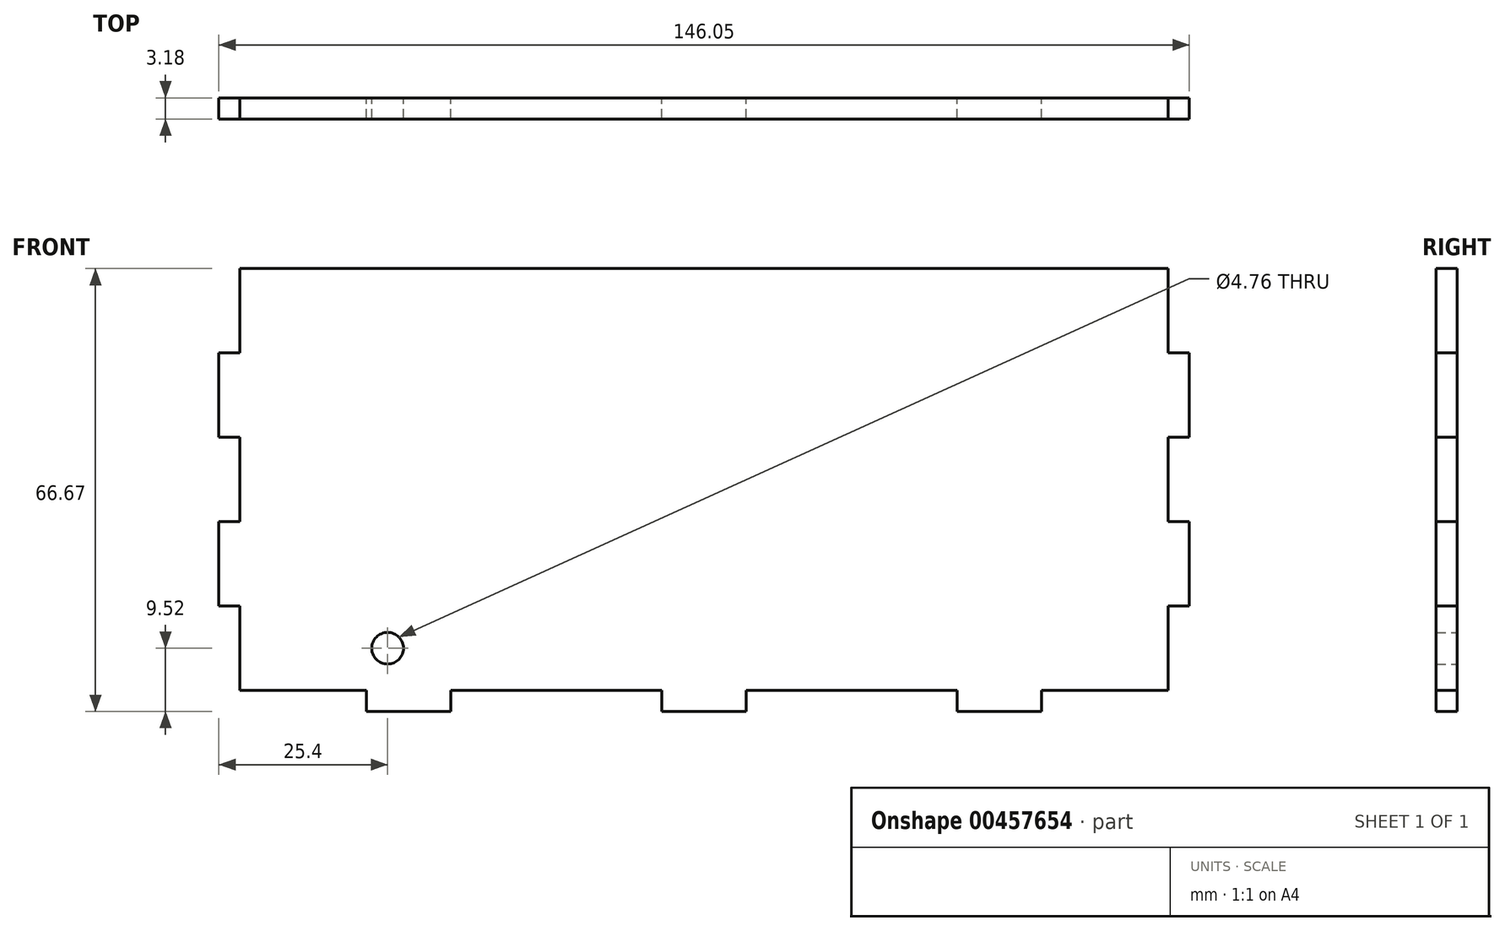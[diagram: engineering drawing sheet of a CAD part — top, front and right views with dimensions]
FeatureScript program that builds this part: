
annotation { "Feature Type Name" : "Feature", "Feature Type Description" : "" }
export const myFeature = defineFeature(function(context is Context, id is Id, definition is map)
    precondition{}
    {
        {
            var Q0;
            Q0=qCreatedBy(makeId("Front.planeOp"),FACE);
            var sketch = newSketch(context, id + "F0", { "sketchPlane" : qUnion([Q0])});
            skLineSegment(sketch, "E0.bottom", {"start": v(-253.3, 200.97) * mm, "end": v(-113.6, 200.97) * mm});
            skLineSegment(sketch, "E0.top", {"start": v(-253.3, 137.47) * mm, "end": v(-234.25, 137.47) * mm});
            skLineSegment(sketch, "E0.left", {"start": v(-253.3, 200.97) * mm, "end": v(-253.3, 188.27) * mm});
            skLineSegment(sketch, "E0.right", {"start": v(-113.6, 200.97) * mm, "end": v(-113.6, 188.27) * mm});
            skLineSegment(sketch, "E1.top", {"start": v(-234.25, 134.3) * mm, "end": v(-221.55, 134.3) * mm});
            skLineSegment(sketch, "E1.left", {"start": v(-234.25, 137.47) * mm, "end": v(-234.25, 134.3) * mm});
            skLineSegment(sketch, "E1.right", {"start": v(-221.55, 137.47) * mm, "end": v(-221.55, 134.3) * mm});
            skLineSegment(sketch, "E2.top", {"start": v(-189.8, 134.3) * mm, "end": v(-177.1, 134.3) * mm});
            skLineSegment(sketch, "E2.left", {"start": v(-189.8, 137.47) * mm, "end": v(-189.8, 134.3) * mm});
            skLineSegment(sketch, "E2.right", {"start": v(-177.1, 137.47) * mm, "end": v(-177.1, 134.3) * mm});
            skLineSegment(sketch, "E3.top", {"start": v(-145.35, 134.3) * mm, "end": v(-132.65, 134.3) * mm});
            skLineSegment(sketch, "E3.left", {"start": v(-145.35, 137.47) * mm, "end": v(-145.35, 134.3) * mm});
            skLineSegment(sketch, "E3.right", {"start": v(-132.65, 137.47) * mm, "end": v(-132.65, 134.3) * mm});
            skLineSegment(sketch, "E4.trimOffspring", {"start": v(-221.55, 137.47) * mm, "end": v(-189.8, 137.47) * mm});
            skLineSegment(sketch, "E5.trimOffspring", {"start": v(-132.65, 137.47) * mm, "end": v(-113.6, 137.47) * mm});
            skLineSegment(sketch, "E6.trimOffspring", {"start": v(-177.1, 137.47) * mm, "end": v(-145.35, 137.47) * mm});
            skLineSegment(sketch, "E7.bottom", {"start": v(-113.6, 188.27) * mm, "end": v(-110.42, 188.27) * mm});
            skLineSegment(sketch, "E7.top", {"start": v(-113.6, 175.57) * mm, "end": v(-110.42, 175.57) * mm});
            skLineSegment(sketch, "E7.right", {"start": v(-110.42, 188.27) * mm, "end": v(-110.42, 175.57) * mm});
            skLineSegment(sketch, "E8.bottom", {"start": v(-113.6, 150.17) * mm, "end": v(-110.42, 150.17) * mm});
            skLineSegment(sketch, "E8.top", {"start": v(-113.6, 162.87) * mm, "end": v(-110.42, 162.87) * mm});
            skLineSegment(sketch, "E8.right", {"start": v(-110.42, 150.17) * mm, "end": v(-110.42, 162.87) * mm});
            skLineSegment(sketch, "E9.bottom", {"start": v(-253.3, 188.27) * mm, "end": v(-256.47, 188.27) * mm});
            skLineSegment(sketch, "E9.top", {"start": v(-253.3, 175.57) * mm, "end": v(-256.47, 175.57) * mm});
            skLineSegment(sketch, "E9.right", {"start": v(-256.47, 188.27) * mm, "end": v(-256.47, 175.57) * mm});
            skLineSegment(sketch, "E10.bottom", {"start": v(-253.3, 162.87) * mm, "end": v(-256.47, 162.87) * mm});
            skLineSegment(sketch, "E10.top", {"start": v(-253.3, 150.17) * mm, "end": v(-256.47, 150.17) * mm});
            skLineSegment(sketch, "E10.right", {"start": v(-256.47, 162.87) * mm, "end": v(-256.47, 150.17) * mm});
            skLineSegment(sketch, "E11.trimOffspring", {"start": v(-253.3, 175.57) * mm, "end": v(-253.3, 162.87) * mm});
            skLineSegment(sketch, "E12.trimOffspring", {"start": v(-253.3, 150.17) * mm, "end": v(-253.3, 137.47) * mm});
            skLineSegment(sketch, "E13.trimOffspring", {"start": v(-113.6, 175.57) * mm, "end": v(-113.6, 162.87) * mm});
            skLineSegment(sketch, "E14.trimOffspring", {"start": v(-113.6, 150.17) * mm, "end": v(-113.6, 137.47) * mm});
            skLineSegment(sketch, "E15", {"start": v(-231.07, 191.57) * mm, "end": v(-231.07, 143.82) * mm});
            skCircle(sketch, "E16", {"center": v(-231.07, 143.82) * mm, "radius": 2.38 * mm});
            skSolve(sketch);
        }
        {
            var Q0;
            Q0 = qSketchRegion(id + "F0", true);
            extrude(context, id + "F1", {"entities" : qUnion([Q0]), "depth" : 3.17 * mm, "offsetDistance" : 25.4 * mm});
        }
    });
